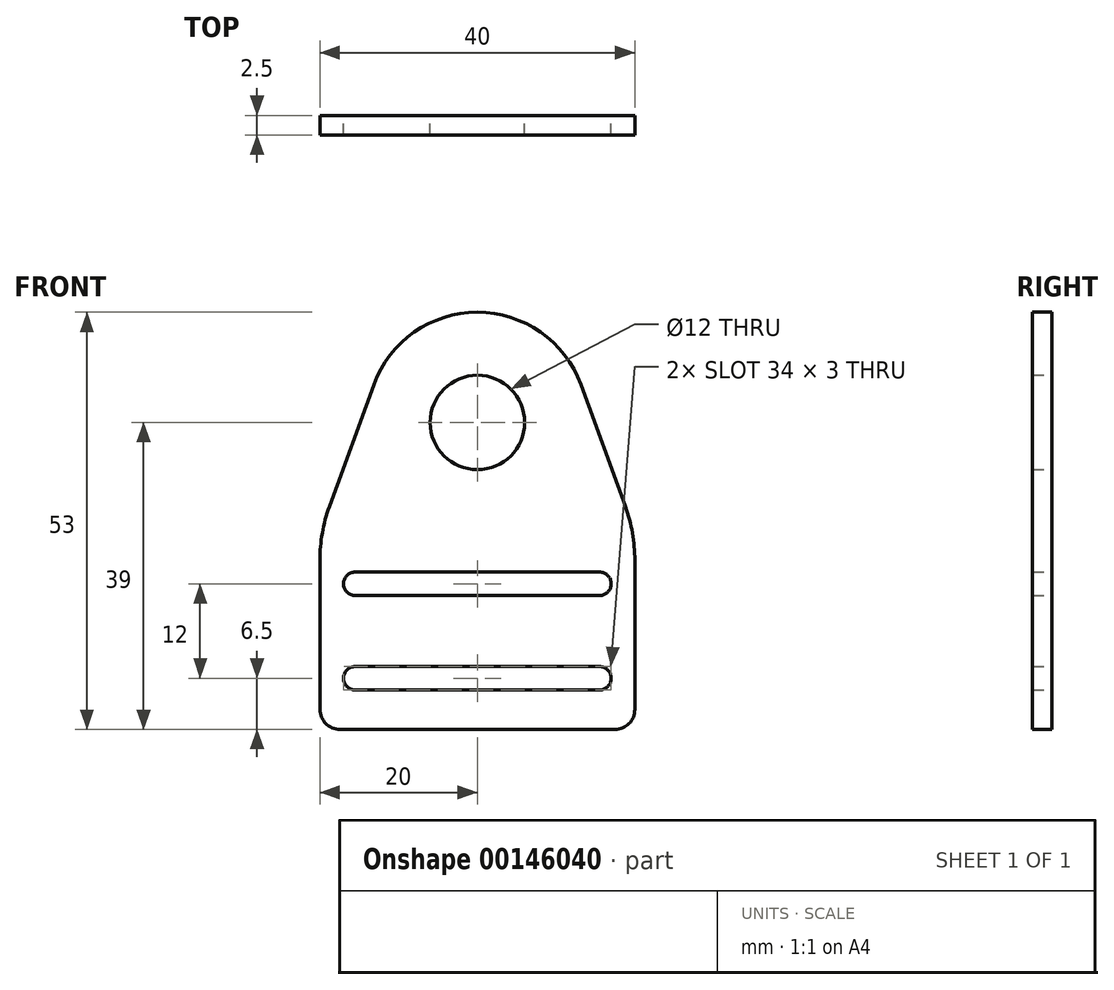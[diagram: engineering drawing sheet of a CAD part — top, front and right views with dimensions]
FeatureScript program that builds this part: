
annotation { "Feature Type Name" : "Feature", "Feature Type Description" : "" }
export const myFeature = defineFeature(function(context is Context, id is Id, definition is map)
    precondition{}
    {
        {
            var Q0;
            Q0=qCreatedBy(makeId("Front.planeOp"),FACE);
            var sketch = newSketch(context, id + "F0", { "sketchPlane" : qUnion([Q0])});
            skLineSegment(sketch, "E0.bottom", {"start": v(-20, 12.5) * mm, "end": v(20, 12.5) * mm, "construction": true});
            skLineSegment(sketch, "E0.top", {"start": v(-17.46, -12.5) * mm, "end": v(17.46, -12.5) * mm});
            skLineSegment(sketch, "E0.left", {"start": v(-20, 8.97) * mm, "end": v(-20, -9.96) * mm});
            skLineSegment(sketch, "E0.right", {"start": v(20, 8.97) * mm, "end": v(20, -9.96) * mm});
            skPoint(sketch, "E0.middle", {"position": v(0, 0) * mm});
            skCircle(sketch, "E1", {"center": v(0, 26.5) * mm, "radius": 6 * mm});
            skArc(sketch, "E2.0", {"start": v(13.15, 31.3) * mm, "mid": v(0, 40.5) * mm, "end": v(-13.15, 31.3) * mm});
            skLineSegment(sketch, "E3", {"start": v(-18.8, 15.82) * mm, "end": v(-13.15, 31.3) * mm});
            skLineSegment(sketch, "E4", {"start": v(18.8, 15.82) * mm, "end": v(13.15, 31.3) * mm});
            skLineSegment(sketch, "E5", {"start": v(-15.5, -4.5) * mm, "end": v(15.5, -4.5) * mm});
            skLineSegment(sketch, "E6", {"start": v(-15.5, -7.5) * mm, "end": v(15.5, -7.5) * mm});
            skArc(sketch, "E7", {"start": v(-15.5, -4.5) * mm, "mid": v(-17, -6) * mm, "end": v(-15.5, -7.5) * mm});
            skArc(sketch, "E8.MirrorCS", {"start": v(15.5, -4.5) * mm, "mid": v(17, -6) * mm, "end": v(15.5, -7.5) * mm});
            skPoint(sketch, "E9.orphan", {"position": v(-20, -7.5) * mm});
            skPoint(sketch, "E10.orphan", {"position": v(20, -7.5) * mm});
            skPoint(sketch, "E11.orphan", {"position": v(20, -4.5) * mm});
            skLineSegment(sketch, "E12.MirrorCS", {"start": v(-15.5, 4.5) * mm, "end": v(15.5, 4.5) * mm});
            skArc(sketch, "E13.MirrorCS", {"start": v(-15.5, 4.5) * mm, "mid": v(-17, 6) * mm, "end": v(-15.5, 7.5) * mm});
            skLineSegment(sketch, "E14.MirrorCS", {"start": v(-15.5, 7.5) * mm, "end": v(15.5, 7.5) * mm});
            skArc(sketch, "E15.MirrorCS", {"start": v(15.5, 4.5) * mm, "mid": v(17, 6) * mm, "end": v(15.5, 7.5) * mm});
            skPoint(sketch, "E16.visualSharp", {"position": v(-20, -12.5) * mm});
            skArc(sketch, "E16.filletArc", {"start": v(-20, -9.96) * mm, "mid": v(-19.26, -11.76) * mm, "end": v(-17.46, -12.5) * mm});
            skPoint(sketch, "E17.visualSharp", {"position": v(20, -12.5) * mm});
            skArc(sketch, "E17.filletArc", {"start": v(17.46, -12.5) * mm, "mid": v(19.26, -11.76) * mm, "end": v(20, -9.96) * mm});
            skPoint(sketch, "E18.visualSharp", {"position": v(20, 12.5) * mm});
            skArc(sketch, "E18.filletArc", {"start": v(20, 8.97) * mm, "mid": v(19.7, 12.45) * mm, "end": v(18.8, 15.82) * mm});
            skPoint(sketch, "E19.visualSharp", {"position": v(-20, 12.5) * mm});
            skArc(sketch, "E19.filletArc", {"start": v(-18.8, 15.82) * mm, "mid": v(-19.7, 12.45) * mm, "end": v(-20, 8.97) * mm});
            skSolve(sketch);
        }
        {
            var Q0;
            Q0=makeQuery(id+"F0.imprint","IMPRINT",FACE,{"disambiguationData":[TD([[makeQuery(id+"F0.imprint","IMPRINT",EDGE,{"derivedFrom":sQuery(id+"F0.wireOp",EDGE,"E0.top")}),1.0]])]});
            extrude(context, id + "F1", {"entities" : qUnion([Q0]), "depth" : 2.5 * mm});
        }
        {
            var Q0;
            Q0=makeQuery(id+"F0.imprint","IMPRINT",FACE,{"disambiguationData":[TD([[makeQuery(id+"F0.imprint","IMPRINT",EDGE,{"derivedFrom":sQuery(id+"F0.wireOp",EDGE,"E1")}),1.0]])]});
            extrude(context, id + "F2", {"entities" : qUnion([Q0]), "depth" : 8 * mm});
        }
        {
            var Q0;
            Q0=makeQuery(id+"F2.opExtrude","CAP_EDGE",EDGE,{"disambiguationData":[OSD([sQuery(id+"F0.wireOp",EDGE,"E1")])],"isStart":false});
            fillet(context, id + "F3", {"entities" : qUnion([Q0]), "radius" : 1.54 * mm, "tangentPropagation" : true, "allowEdgeOverflow" : false});
        }
        {
            var Q0;
            Q0=makeQuery(id+"F2.opExtrude","SWEPT_BODY",BODY,{"disambiguationData":[OSD([sQuery(id+"F0.wireOp",EDGE,"E1")])]});
            deleteBodies(context, id + "F4", {"entities" : qUnion([Q0])});
        }
    });
